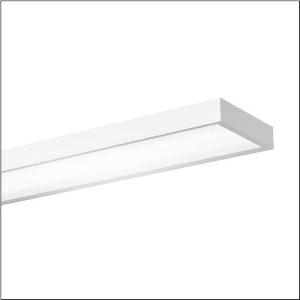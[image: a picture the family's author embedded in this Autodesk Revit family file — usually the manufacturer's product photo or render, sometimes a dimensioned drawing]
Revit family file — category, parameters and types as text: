
# Revit family: sport_31_51hs12dd4gca
name_source: partatom
category: Lighting Fixtures
units: mm (PartAtom-declared; Revit-internal decimal feet)

## family parameters
Cut with Voids When Loaded = No
Host = Face
Light Source = No
Part Type = Normal
Room Calculation Point = No
Round Connector Dimension = Use Diameter
Shared = No

## types (1)
- --- (1 x LED, 15290 lm, 113 W, 4000K)
    Apparent Load = 113 VA
    CIE Flux Codes = 65 89 97 100 100
    Color Rendering = 80
    Color Temperature = 4000K
    Default Elevation = 1800 mm
    Description = Sport 31, high bay luminaire, primary light control with reflector, of sheet steel, primary anti-glare with prismatic structure, of PC, primary optical cover: cover panel, of PC, light emission: direct distribution, primary light characteristic: symmetric, installation type: suspended mounting, recessed, surface-mounted, LED, rated luminous flux: 16.000lm, luminous efficacy: 137lm/W, light colour: 840, colour temperature: 4000K, control gear: DALI 2, with terminal, 5-pole, max. 2.5mm², mains connection: 220..240V, AC/DC, 50/60Hz, rated input power: 117W, housing, of sheet steel, traffic white (RAL 9016), length: 1.540mm, width: 415mm, height: 95mm, protection rating (complete): IP20, protection rating (lamp compartment, on room side): IP50, insulation class (complete): insulation class I (protective earthing), certification: CE, ENEC, UKCA, ball protection: ball impact resistant with ceiling mounting or chain suspension, impact resistance: IK08, permissible operating ambient temperature: -20..+35°C, standard: DIN 18032-3, EN 60598-2-22, packaging unit: 1 piece
    Height = 100 mm  [stored 0.328084 ft]
    Lamp = 1 x LED
    Lamp Light Flux = 15290 lm
    Lamp Power = 113 W
    Lamp count = 1
    Length = 1500 mm
    Luminous efficacy = 135 lm/W
    Manufacturer = Siteco
    ModVariant = No
    Model = 51HS12DD4GCA
    Mounting Place = Ceiling
    Mounting Type = Pendant
    Number of Poles = 1
    OnlyDefault = Yes
    Power Factor = 1
    Product Name = Sport 31
    Product group = high bay luminaire
    ProductGroupID = 902
    Protection Class = Protection class I
    Protection Degree = IP 20
    RLX_Detail_Level = 1
    RLX_Emergency_Light_Flux = 0 lm
    RLX_Emergency_Type = 0
    RLX_Emergency_Type_DB = No
    RlxData = <blob elided: 24077 chars, md5=4039dbbf>
    Socket = socket
    Standby Power = 0 W
    System Light Flux = 15290 lm
    System Power = 113 W
    Type Comments = factory setting: luminous flux: 100 % | dim-lin: 254 | 558 mA
    Type Image = l_1397495.jpg
    URL = http://relux.com
    VarID = @adj_196169
    Voltage = 0 V
    Weight = 0.00 kg
    Width = 415 mm

note: [stored X ft] marks values corroborated as IEEE doubles in the binary element streams (Revit-internal decimal feet)

## geometry (parser evidence)
native form markers: Blend x4, Sweep x12
no freeform markers — native parametric forms only
